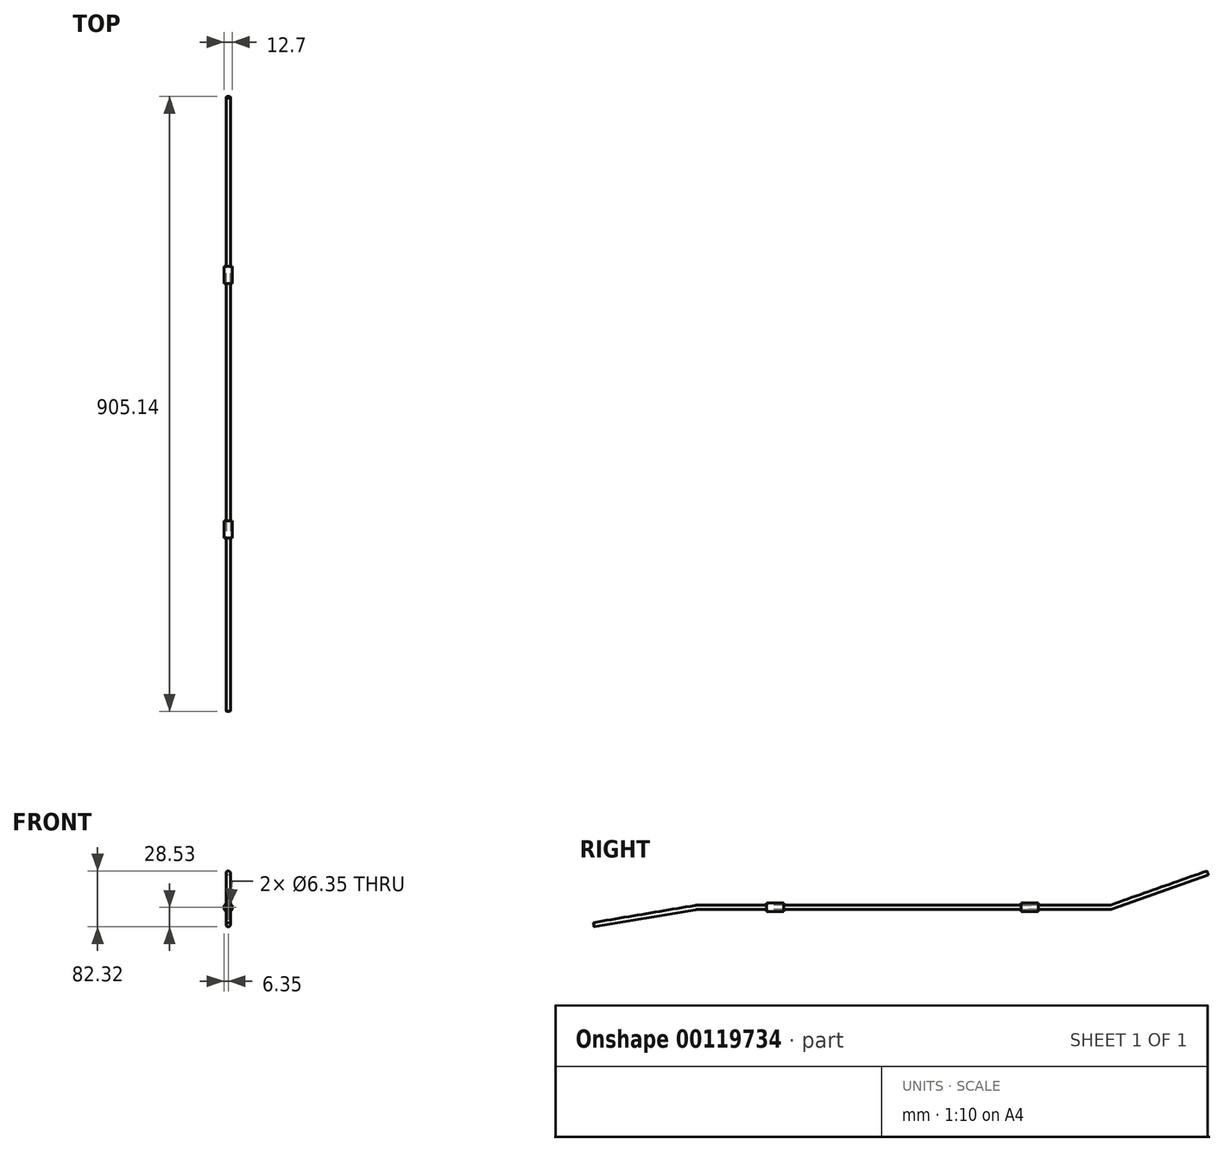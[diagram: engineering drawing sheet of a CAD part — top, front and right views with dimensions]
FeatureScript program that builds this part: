
annotation { "Feature Type Name" : "Feature", "Feature Type Description" : "" }
export const myFeature = defineFeature(function(context is Context, id is Id, definition is map)
    precondition{}
    {
        {
            var Q0;
            Q0=qCreatedBy(makeId("Right.planeOp"),FACE);
            var sketch = newSketch(context, id + "F0", { "sketchPlane" : qUnion([Q0])});
            skLineSegment(sketch, "E0", {"start": v(-303.18, 0) * mm, "end": v(303.18, 0) * mm});
            skLineSegment(sketch, "E1", {"start": v(307.41, 0.73) * mm, "end": v(449.04, 50.8) * mm});
            skLineSegment(sketch, "E2", {"start": v(-305.3, -0.18) * mm, "end": v(-454.51, -25.4) * mm});
            skPoint(sketch, "E3.visualSharp", {"position": v(305.36, 0) * mm});
            skArc(sketch, "E3.filletArc", {"start": v(303.18, 0) * mm, "mid": v(305.33, 0.18) * mm, "end": v(307.41, 0.73) * mm});
            skPoint(sketch, "E4.visualSharp", {"position": v(-304.24, 0) * mm});
            skArc(sketch, "E4.filletArc", {"start": v(-303.18, 0) * mm, "mid": v(-304.24, -0.04) * mm, "end": v(-305.3, -0.18) * mm});
            skSolve(sketch);
        }
        {
            var Q0;
            Q0=sQuery(id+"F0.wireOp",VERTEX,"E1.end");
            var Q1;
            Q1=sQuery(id+"F0.wireOp",EDGE,"E1");
            cPlane(context, id + "F1", {"entities" : qUnion([Q0, Q1]), "cplaneType" : CPlaneType.LINE_POINT, "offset" : 150 * mm, "width" : 150 * mm, "height" : 150 * mm});
        }
        {
            var Q0;
            Q0=qCreatedBy(id+"F1.planeOp",FACE);
            var sketch = newSketch(context, id + "F2", { "sketchPlane" : qUnion([Q0])});
            skPoint(sketch, "E5.0", {"position": v(0, -101.79) * mm});
            skCircle(sketch, "E6", {"center": v(0, -101.79) * mm, "radius": 3.18 * mm});
            skSolve(sketch);
        }
        {
            var Q0;
            Q0=makeQuery(id+"F2.imprint","IMPRINT",FACE,{"disambiguationData":[TD([[makeQuery(id+"F2.imprint","IMPRINT",EDGE,{"derivedFrom":sQuery(id+"F2.wireOp",EDGE,"E6")}),1.0]])]});
            var Q1;
            Q1=sQuery(id+"F0.wireOp",EDGE,"E1");
            var Q2;
            Q2=sQuery(id+"F0.wireOp",EDGE,"E3.filletArc");
            var Q3;
            Q3=sQuery(id+"F0.wireOp",EDGE,"E0");
            var Q4;
            Q4=sQuery(id+"F0.wireOp",EDGE,"E4.filletArc");
            var Q5;
            Q5=sQuery(id+"F0.wireOp",EDGE,"E2");
            sweep(context, id + "F3", {"profiles" : qUnion([Q0]), "path" : qUnion([Q1, Q2, Q3, Q4, Q5])});
        }
        {
            var Q0;
            Q0=qCreatedBy(makeId("Front.planeOp"),FACE);
            var sketch = newSketch(context, id + "F4", { "sketchPlane" : qUnion([Q0])});
            skCircle(sketch, "E7", {"center": v(0, 0) * mm, "radius": 3.18 * mm});
            skCircle(sketch, "E8", {"center": v(0, 0) * mm, "radius": 6.35 * mm});
            skSolve(sketch);
        }
        {
            var Q0;
            Q0=qSketchRegion(id+"F4",true);
            extrude(context, id + "F5", {"entities" : qUnion([Q0]), "depth" : 25.4 * mm});
        }
        {
            var Q0;
            Q0=makeQuery(id+"F5.opExtrude","SWEPT_BODY",BODY,{"disambiguationData":[OSD([sQuery(id+"F4.wireOp",EDGE,"E7"),sQuery(id+"F4.wireOp",EDGE,"E8")])]});
            transform(context, id + "F6", {"entities" : qUnion([Q0]), "transformType" : TransformType.TRANSLATION_3D, "dx" : 0 * mm, "dy" : 200 * mm, "dz" : 0 * mm, "makeCopy" : false});
        }
        {
            var Q0;
            Q0=makeQuery(id+"F5.opExtrude","SWEPT_BODY",BODY,{"disambiguationData":[OSD([sQuery(id+"F4.wireOp",EDGE,"E7"),sQuery(id+"F4.wireOp",EDGE,"E8")])]});
            var Q1;
            Q1=qCreatedBy(makeId("Front.planeOp"),FACE);
            mirror(context, id + "F7", {"entities" : qUnion([Q0]), "mirrorPlane" : qUnion([Q1])});
        }
        {
            var Q0;
            Q0=qCreatedBy(makeId("Front.planeOp"),FACE);
            var sketch = newSketch(context, id + "F8", { "sketchPlane" : qUnion([Q0])});
            skLineSegment(sketch, "E9", {"start": v(0, 0) * mm, "end": v(-6.35, 0) * mm});
            skSolve(sketch);
        }
    });
